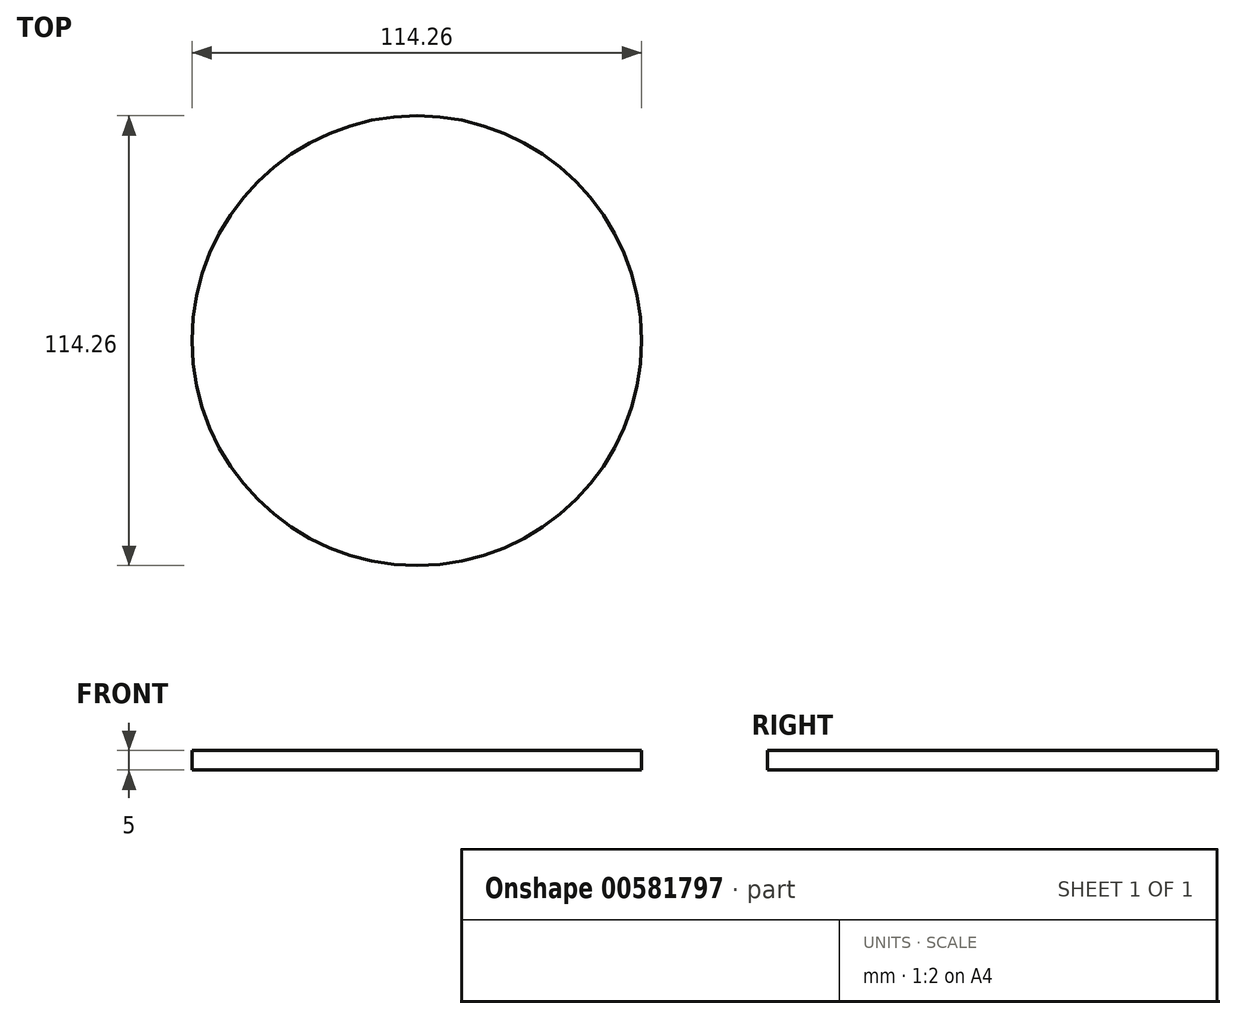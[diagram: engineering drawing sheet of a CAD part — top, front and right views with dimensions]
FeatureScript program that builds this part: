
annotation { "Feature Type Name" : "Feature", "Feature Type Description" : "" }
export const myFeature = defineFeature(function(context is Context, id is Id, definition is map)
    precondition{}
    {
        {
            var Q0;
            Q0=qCreatedBy(makeId("Top.planeOp"),FACE);
            var sketch = newSketch(context, id + "F0", { "sketchPlane" : qUnion([Q0])});
            skCircle(sketch, "E0", {"center": v(0, 0) * mm, "radius": 57.13 * mm});
            skSolve(sketch);
        }
        {
            var Q0;
            Q0=makeQuery(id+"F0.imprint","IMPRINT",FACE,{"disambiguationData":[TD([[makeQuery(id+"F0.imprint","IMPRINT",EDGE,{"derivedFrom":sQuery(id+"F0.wireOp",EDGE,"E0")}),1.0]])]});
            extrude(context, id + "F1", {"entities" : qUnion([Q0]), "depth" : 5 * mm, "offsetDistance" : 25.4 * mm});
        }
    });
